# Revit family: Lavatory_Faucet-GROHE-ATRIO-23831_Series
name_source: partatom
category: Plumbing Fixtures
revit_build: Autodesk Revit 2014 (Build: 20130308_1515(x64)
units: mm (PartAtom-declared; Revit-internal decimal feet)

## types (2) — shared parameters
ADA Compliant = Yes
Assembly Code = D2020300
CW Connection = Yes
CWFU = 3
Cold Water Connection Diameter = 3/8"
Default Elevation = 0"
Description = Atrio Single-Handle Bathroom Faucet M-Size
Flow Rate = 1.2 gpm (4.5/min)
HW Connection = Yes
HWFU = 3
Height = 9 3/16"
Hot Water Connection Diameter = 0"
Installation Type = Surface Mounted
Length = 4 15/16"
Manufacturer = GROHE
Price = Prices may vary. Please consult Manufacturer Representative for most up-to-date price list.
Product Page URL = https://www.grohe.us
URL = https://www.grohe.us
Vent Connection = No
WFU = 4
Warranty Documentation Link = https://cdn.cloud.grohe.com
Waste Connection = No
Width = 1 15/16"
cUPC Compliant = Yes

## per-type parameters (varying)
| type | Finish | Material |
| 23831003 | Metal-Grohe-003-Chrome | Metal-Grohe-003-Chrome |
| 23831EN3 | Metal-Grohe-EN3-Brushed Nickel | Metal-Grohe-EN3-Brushed Nickel |

note: column(s) folded — value = type name in every type: Model

## geometry (parser evidence)
native form markers: Sweep x1
no freeform markers — native parametric forms only
